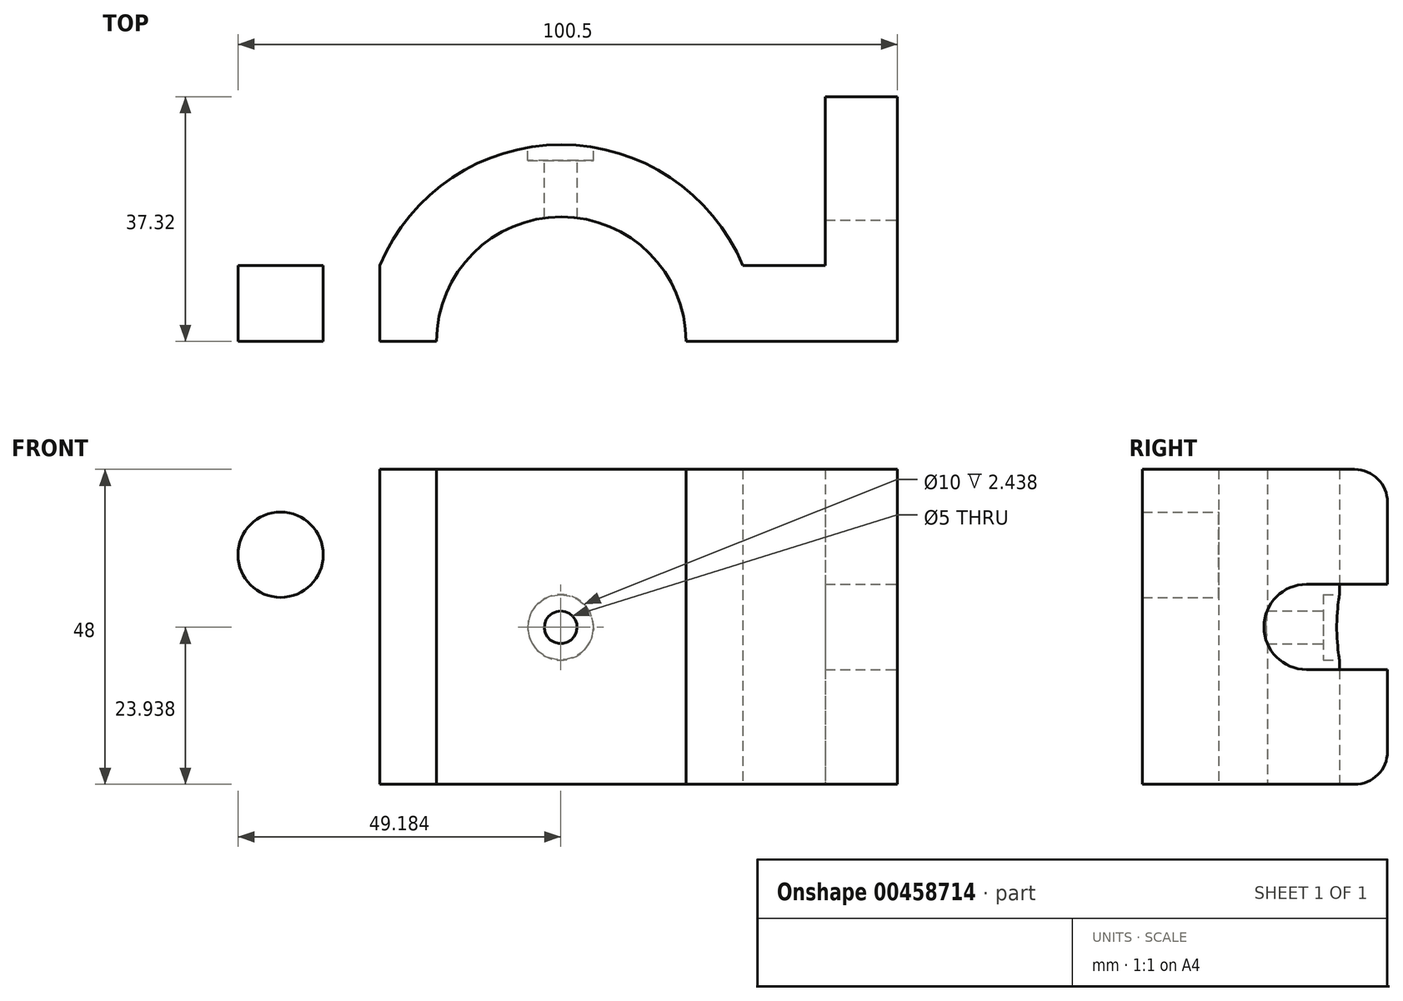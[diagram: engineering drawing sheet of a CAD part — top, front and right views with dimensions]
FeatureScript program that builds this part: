
annotation { "Feature Type Name" : "Feature", "Feature Type Description" : "" }
export const myFeature = defineFeature(function(context is Context, id is Id, definition is map)
    precondition{}
    {
        {
            var Q0;
            Q0=qCreatedBy(makeId("Top.planeOp"),FACE);
            var sketch = newSketch(context, id + "F0", { "sketchPlane" : qUnion([Q0])});
            skLineSegment(sketch, "E0", {"start": v(-36.77, 12.22) * mm, "end": v(-36.77, 0) * mm});
            skLineSegment(sketch, "E1", {"start": v(-36.77, 0) * mm, "end": v(0, 0) * mm});
            skArc(sketch, "E2", {"start": v(0, 0) * mm, "mid": v(19, 19) * mm, "end": v(38, 0) * mm});
            skLineSegment(sketch, "E3", {"start": v(-8.68, 11.57) * mm, "end": v(-36.77, 11.57) * mm});
            skPoint(sketch, "E3.endSnap0", {"position": v(-36.77, 6.1) * mm});
            skArc(sketch, "E4", {"start": v(-8.68, 11.57) * mm, "mid": v(19, 30) * mm, "end": v(46.68, 11.57) * mm});
            skLineSegment(sketch, "E5", {"start": v(46.68, 11.57) * mm, "end": v(59.23, 11.57) * mm});
            skLineSegment(sketch, "E6", {"start": v(38, 0) * mm, "end": v(70.23, 0) * mm});
            skLineSegment(sketch, "E7", {"start": v(59.23, 11.57) * mm, "end": v(59.23, 37.32) * mm});
            skLineSegment(sketch, "E8", {"start": v(70.23, 37.32) * mm, "end": v(70.23, 0) * mm});
            skLineSegment(sketch, "E9", {"start": v(59.23, 37.32) * mm, "end": v(70.23, 37.32) * mm});
            skLineSegment(sketch, "E10", {"start": v(19, 0) * mm, "end": v(19, 30) * mm, "construction": true});
            skPoint(sketch, "E11", {"position": v(19, 30) * mm});
            skSolve(sketch);
        }
        {
            var Q0;
            {var subQ1=sQuery(id+"F0.wireOp",EDGE,"E1");Q0=makeQuery(id+"F0.imprint","IMPRINT",FACE,{"disambiguationData":[TD([[makeQuery(id+"F0.imprint","IMPRINT",EDGE,{"derivedFrom":subQ1}),1.0]])]});}
            extrude(context, id + "F1", {"entities" : qUnion([Q0]), "depth" : 48 * mm});
        }
        {
            var Q0;
            Q0=makeQuery(id+"F1.opExtrude","CAP_EDGE",EDGE,{"disambiguationData":[OSD([sQuery(id+"F0.wireOp",EDGE,"E9")])],"isStart":false});
            var Q1;
            Q1=makeQuery(id+"F1.opExtrude","CAP_EDGE",EDGE,{"disambiguationData":[OSD([sQuery(id+"F0.wireOp",EDGE,"E9")])],"isStart":true});
            fillet(context, id + "F2", {"entities" : qUnion([Q0, Q1]), "radius" : 5 * mm, "tangentPropagation" : true, "allowEdgeOverflow" : false});
        }
        {
            var Q0;
            Q0=makeQuery(id+"F1.opExtrude","SWEPT_FACE",FACE,{"disambiguationData":[OSD([sQuery(id+"F0.wireOp",EDGE,"E8")])]});
            var sketch = newSketch(context, id + "F3", { "sketchPlane" : qUnion([Q0])});
            skLineSegment(sketch, "E12", {"start": v(37.32, 30.5) * mm, "end": v(25, 30.5) * mm});
            skLineSegment(sketch, "E13", {"start": v(37.32, 17.5) * mm, "end": v(25, 17.5) * mm});
            skArc(sketch, "E14", {"start": v(25, 17.5) * mm, "mid": v(18.5, 24) * mm, "end": v(25, 30.5) * mm});
            skArc(sketch, "E15", {"start": v(25, 30.5) * mm, "mid": v(18.5, 24) * mm, "end": v(25, 17.5) * mm});
            skLineSegment(sketch, "E16", {"start": v(37.32, 24) * mm, "end": v(0, 24) * mm, "construction": true});
            skLineSegment(sketch, "E17", {"start": v(0, 48) * mm, "end": v(0, 0) * mm});
            skSolve(sketch);
        }
        {
            var Q0;
            Q0 = qSketchRegion(id + "F3", true);
            var Q1;
            {var subQ0=sQuery(id+"F3.wireOp",EDGE,"E12");Q1=makeQuery(id+"F3.imprint","IMPRINT",FACE,{"disambiguationData":[TD([[makeQuery(id+"F3.imprint","IMPRINT",EDGE,{"derivedFrom":subQ0}),1.0]])]});}
            extrude(context, id + "F4", {"entities" : qUnion([Q0, Q1]), "operationType" : NewBodyOperationType.REMOVE, "oppositeDirection" : true, "depth" : 11 * mm});
        }
        {
            var Q0;
            Q0=makeQuery(id+"F1.opExtrude","CAP_EDGE",EDGE,{"disambiguationData":[OSD([sQuery(id+"F0.wireOp",EDGE,"E0")])],"isStart":false});
            var Q1;
            Q1=makeQuery(id+"F1.opExtrude","CAP_EDGE",EDGE,{"disambiguationData":[OSD([sQuery(id+"F0.wireOp",EDGE,"E0")])],"isStart":true});
            fillet(context, id + "F5", {"entities" : qUnion([Q0, Q1]), "radius" : 13 * mm, "tangentPropagation" : true, "allowEdgeOverflow" : false});
        }
        {
            var Q0;
            Q0=makeQuery(id+"F1.opExtrude","SWEPT_FACE",FACE,{"disambiguationData":[OSD([sQuery(id+"F0.wireOp",EDGE,"E3")])]});
            var sketch = newSketch(context, id + "F6", { "sketchPlane" : qUnion([Q0])});
            skCircle(sketch, "E18", {"center": v(23.77, 13) * mm, "radius": 6.5 * mm});
            skLineSegment(sketch, "E19", {"start": v(36.77, 24) * mm, "end": v(8.68, 24) * mm, "construction": true});
            skCircle(sketch, "E20.MirrorC", {"center": v(23.77, 35) * mm, "radius": 6.5 * mm});
            skSolve(sketch);
        }
        {
            var Q0;
            Q0=makeQuery(id+"F6.imprint","IMPRINT",FACE,{"disambiguationData":[TD([[makeQuery(id+"F6.imprint","IMPRINT",EDGE,{"derivedFrom":sQuery(id+"F6.wireOp",EDGE,"E18")}),1.0]])]});
            var Q1;
            Q1=makeQuery(id+"F6.imprint","IMPRINT",FACE,{"disambiguationData":[TD([[makeQuery(id+"F6.imprint","IMPRINT",EDGE,{"derivedFrom":sQuery(id+"F6.wireOp",EDGE,"E20.MirrorC")}),-1.0]])]});
            extrude(context, id + "F7", {"entities" : qUnion([Q0, Q1]), "operationType" : NewBodyOperationType.REMOVE, "oppositeDirection" : true, "depth" : 25 * mm});
        }
        {
            var Q0;
            Q0=qCreatedBy(makeId("Front.planeOp"),FACE);
            cPlane(context, id + "F8", {"entities" : qUnion([Q0]), "cplaneType" : CPlaneType.OFFSET, "offset" : 30 * mm, "oppositeDirection" : true, "width" : 150 * mm, "height" : 150 * mm});
        }
        {
            var Q0;
            Q0=qCreatedBy(id+"F8.planeOp",FACE);
            var sketch = newSketch(context, id + "F9", { "sketchPlane" : qUnion([Q0])});
            skLineSegment(sketch, "E21", {"start": v(18.91, 23.94) * mm, "end": v(18.91, 0) * mm});
            skLineSegment(sketch, "E22", {"start": v(18.91, 0) * mm, "end": v(18.91, 23.94) * mm});
            skLineSegment(sketch, "E23", {"start": v(18.91, 23.94) * mm, "end": v(18.91, 48.1) * mm});
            skPoint(sketch, "E24", {"position": v(18.91, 23.94) * mm});
            skSolve(sketch);
        }
        {
            var Q0;
            Q0=sQuery(id+"F9.wireOp",VERTEX,"E24");
            var Q1;
            Q1=makeQuery(id+"F1.opExtrude","SWEPT_BODY",BODY,{"disambiguationData":[OSD([sQuery(id+"F0.wireOp",EDGE,"E0"),sQuery(id+"F0.wireOp",EDGE,"E1"),sQuery(id+"F0.wireOp",EDGE,"E2"),sQuery(id+"F0.wireOp",EDGE,"E3"),sQuery(id+"F0.wireOp",EDGE,"E4"),sQuery(id+"F0.wireOp",EDGE,"E5"),sQuery(id+"F0.wireOp",EDGE,"E6"),sQuery(id+"F0.wireOp",EDGE,"E7"),sQuery(id+"F0.wireOp",EDGE,"E8"),sQuery(id+"F0.wireOp",EDGE,"E9")])]});
            hole(context, id + "F10", {"style" : HoleStyle.C_BORE, "endStyle" : HoleEndStyle.THROUGH, "oppositeDirection" : true, "holeDiameter" : 5 * mm, "cBoreDiameter" : 10 * mm, "cBoreDepth" : 2 * mm, "tappedDepth" : 12 * mm, "tapClearance" : 3, "locations" : qUnion([Q0]), "scope" : qUnion([Q1])});
        }
    });
